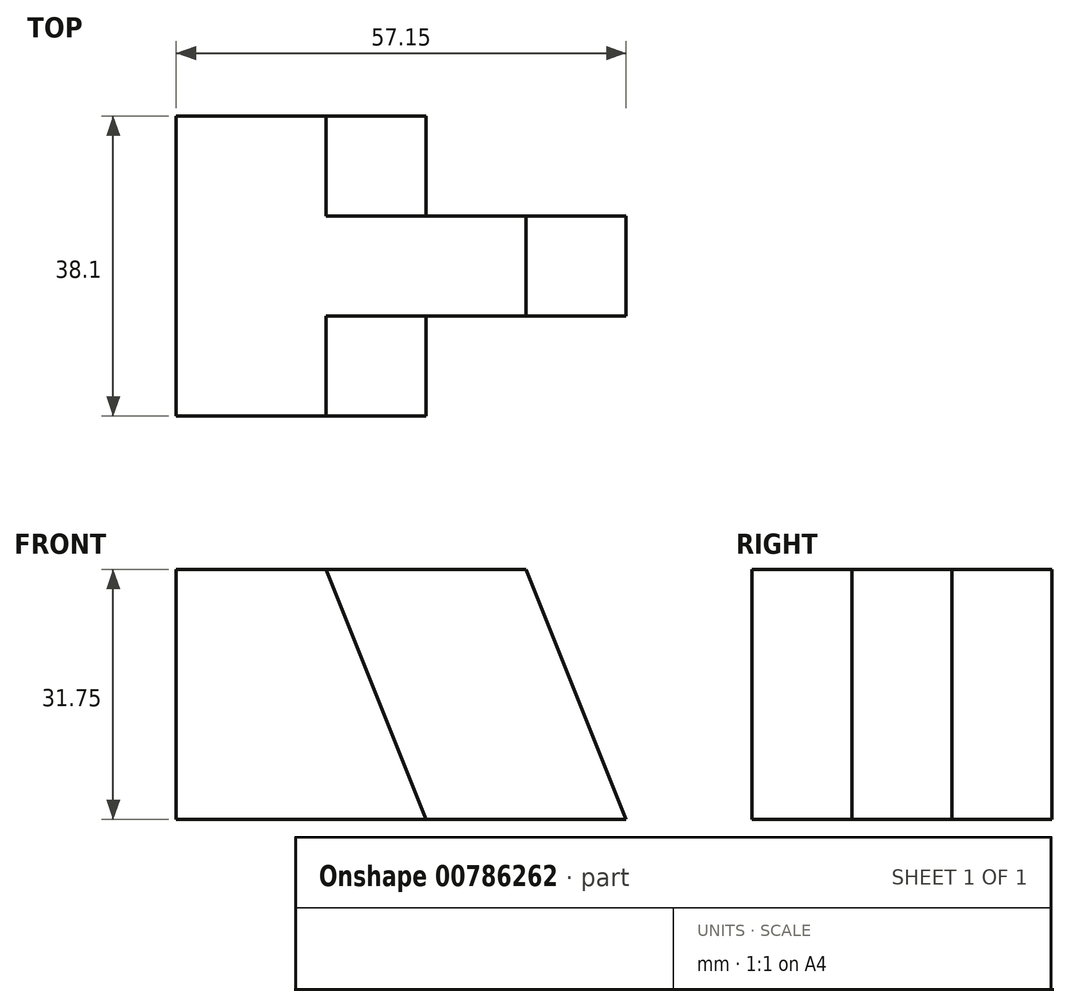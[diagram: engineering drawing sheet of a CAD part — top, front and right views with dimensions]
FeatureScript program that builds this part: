
annotation { "Feature Type Name" : "Feature", "Feature Type Description" : "" }
export const myFeature = defineFeature(function(context is Context, id is Id, definition is map)
    precondition{}
    {
        {
            var Q0;
            Q0=qCreatedBy(makeId("Top.planeOp"),FACE);
            var sketch = newSketch(context, id + "F0", { "sketchPlane" : qUnion([Q0])});
            skLineSegment(sketch, "E0", {"start": v(0, 0) * mm, "end": v(31.75, 0) * mm});
            skLineSegment(sketch, "E1", {"start": v(31.75, 0) * mm, "end": v(31.75, 12.7) * mm});
            skLineSegment(sketch, "E2", {"start": v(31.75, 12.7) * mm, "end": v(57.15, 12.7) * mm});
            skLineSegment(sketch, "E3", {"start": v(57.15, 12.7) * mm, "end": v(57.15, 25.4) * mm});
            skLineSegment(sketch, "E4", {"start": v(57.15, 25.4) * mm, "end": v(31.75, 25.4) * mm});
            skLineSegment(sketch, "E5", {"start": v(31.75, 25.4) * mm, "end": v(31.75, 38.1) * mm});
            skLineSegment(sketch, "E6", {"start": v(31.75, 38.1) * mm, "end": v(0, 38.1) * mm});
            skLineSegment(sketch, "E7", {"start": v(0, 38.1) * mm, "end": v(0, 0) * mm});
            skSolve(sketch);
        }
        {
            var Q0;
            Q0 = qSketchRegion(id + "F0", true);
            extrude(context, id + "F1", {"entities" : qUnion([Q0]), "depth" : 31.75 * mm, "offsetDistance" : 25.4 * mm});
        }
        {
            var Q0;
            Q0=makeQuery(id+"F1.opExtrude","SWEPT_FACE",FACE,{"disambiguationData":[OSD([sQuery(id+"F0.wireOp",EDGE,"E0")])]});
            var sketch = newSketch(context, id + "F2", { "sketchPlane" : qUnion([Q0])});
            skLineSegment(sketch, "E8", {"start": v(31.75, 31.75) * mm, "end": v(19.05, 31.75) * mm});
            skLineSegment(sketch, "E9", {"start": v(19.05, 31.75) * mm, "end": v(31.75, 0) * mm});
            skSolve(sketch);
        }
        {
            var Q0;
            Q0=makeQuery(id+"F2.imprint","IMPRINT",FACE,{"disambiguationData":[TD([[makeQuery(id+"F2.imprint","IMPRINT",EDGE,{"derivedFrom":sQuery(id+"F2.wireOp",EDGE,"E8")}),-1.0]])]});
            extrude(context, id + "F3", {"entities" : qUnion([Q0]), "operationType" : NewBodyOperationType.REMOVE, "oppositeDirection" : true, "depth" : 12.7 * mm, "offsetDistance" : 25.4 * mm});
        }
        {
            var Q0;
            Q0=makeQuery(id+"F3.boolean.opBoolean","MERGE",FACE,{"derivedFrom":[makeQuery(id+"F1.opExtrude","SWEPT_FACE",FACE,{"disambiguationData":[OSD([sQuery(id+"F0.wireOp",EDGE,"E2")])]}),makeQuery(id+"F3.opExtrude","CAP_FACE",FACE,{"disambiguationData":[OSD([sQuery(id+"F0.wireOp",EDGE,"E0"),sQuery(id+"F0.wireOp",EDGE,"E1"),sQuery(id+"F2.wireOp",EDGE,"E8"),sQuery(id+"F2.wireOp",EDGE,"E9")])],"isStart":false})]});
            var sketch = newSketch(context, id + "F4", { "sketchPlane" : qUnion([Q0])});
            skLineSegment(sketch, "E10", {"start": v(57.15, 31.75) * mm, "end": v(44.45, 31.75) * mm});
            skLineSegment(sketch, "E11", {"start": v(57.15, 0) * mm, "end": v(44.45, 31.75) * mm});
            skSolve(sketch);
        }
        {
            var Q0;
            Q0=makeQuery(id+"F4.imprint","IMPRINT",FACE,{"disambiguationData":[TD([[makeQuery(id+"F4.imprint","IMPRINT",EDGE,{"derivedFrom":sQuery(id+"F4.wireOp",EDGE,"E10")}),-1.0]])]});
            extrude(context, id + "F5", {"entities" : qUnion([Q0]), "operationType" : NewBodyOperationType.REMOVE, "oppositeDirection" : true, "depth" : 12.7 * mm, "offsetDistance" : 25.4 * mm});
        }
        {
            var Q0;
            Q0=makeQuery(id+"F1.opExtrude","SWEPT_FACE",FACE,{"disambiguationData":[OSD([sQuery(id+"F0.wireOp",EDGE,"E6")])]});
            var sketch = newSketch(context, id + "F6", { "sketchPlane" : qUnion([Q0])});
            skLineSegment(sketch, "E12", {"start": v(-31.75, 31.75) * mm, "end": v(-19.05, 31.75) * mm});
            skLineSegment(sketch, "E13", {"start": v(-31.75, 0) * mm, "end": v(-19.05, 31.75) * mm});
            skSolve(sketch);
        }
        {
            var Q0;
            Q0=makeQuery(id+"F6.imprint","IMPRINT",FACE,{"disambiguationData":[TD([[makeQuery(id+"F6.imprint","IMPRINT",EDGE,{"derivedFrom":sQuery(id+"F6.wireOp",EDGE,"E12")}),-1.0]])]});
            extrude(context, id + "F7", {"entities" : qUnion([Q0]), "operationType" : NewBodyOperationType.REMOVE, "oppositeDirection" : true, "depth" : 12.7 * mm, "offsetDistance" : 25.4 * mm});
        }
    });
